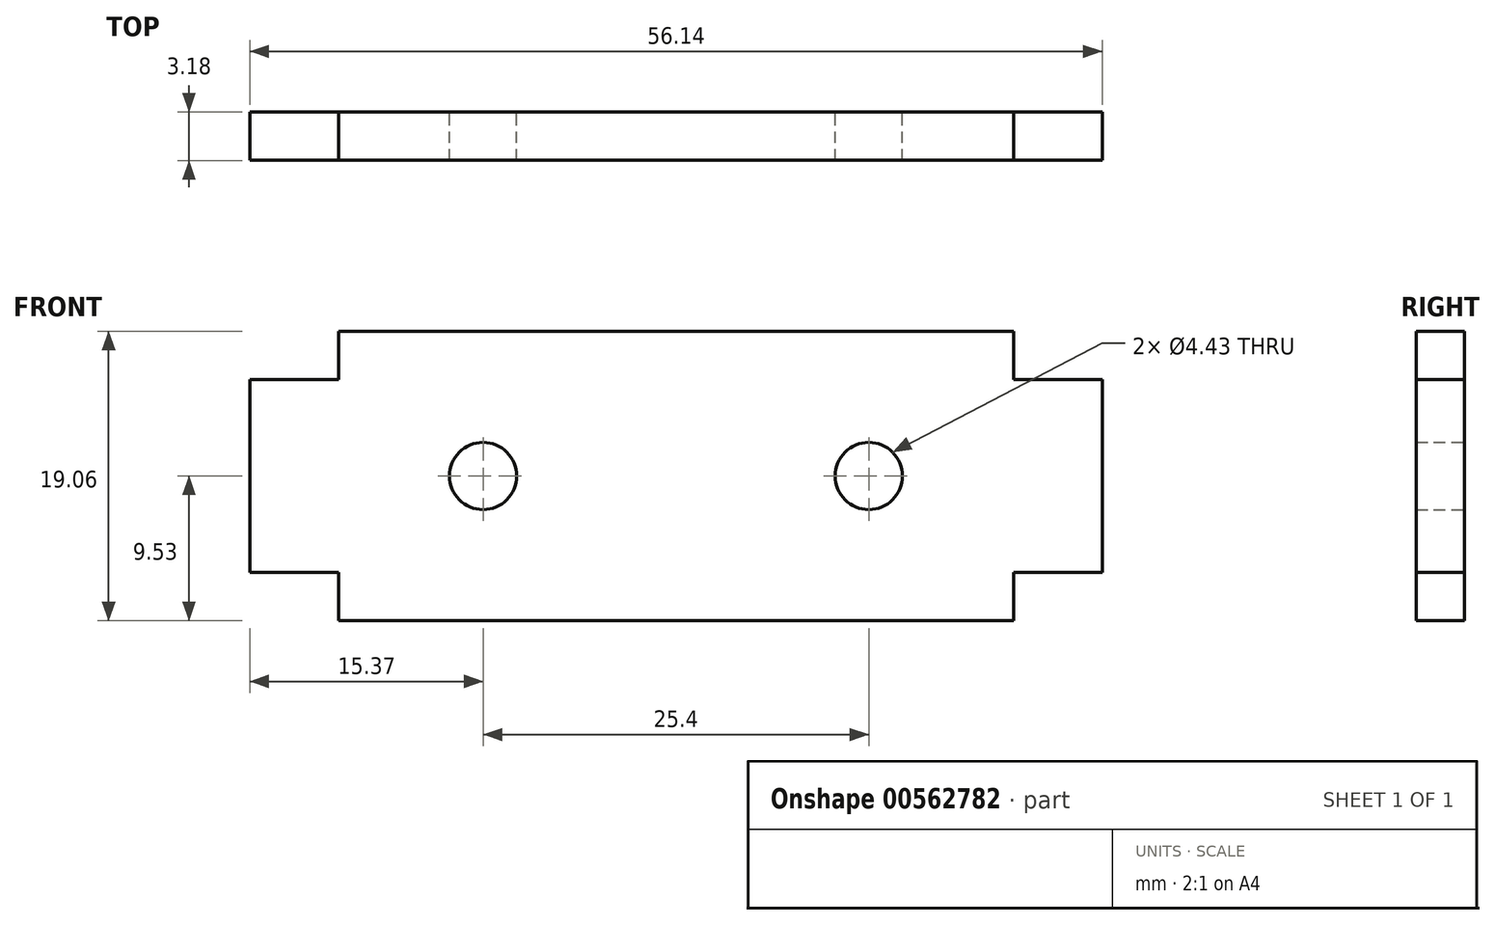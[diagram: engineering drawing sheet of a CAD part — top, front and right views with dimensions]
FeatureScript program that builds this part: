
annotation { "Feature Type Name" : "Feature", "Feature Type Description" : "" }
export const myFeature = defineFeature(function(context is Context, id is Id, definition is map)
    precondition{}
    {
        {
            var Q0;
            Q0=qCreatedBy(makeId("Front.planeOp"),FACE);
            var sketch = newSketch(context, id + "F0", { "sketchPlane" : qUnion([Q0])});
            skLineSegment(sketch, "E0.bottom", {"start": v(-22.23, 9.53) * mm, "end": v(22.23, 9.53) * mm});
            skLineSegment(sketch, "E0.top", {"start": v(-22.23, -9.52) * mm, "end": v(22.23, -9.52) * mm});
            skLineSegment(sketch, "E0.left", {"start": v(-22.23, 9.53) * mm, "end": v(-22.23, 6.35) * mm});
            skLineSegment(sketch, "E0.right", {"start": v(22.23, 9.53) * mm, "end": v(22.23, 6.35) * mm});
            skPoint(sketch, "E0.middle", {"position": v(0, 0) * mm});
            skCircle(sketch, "E1", {"center": v(-12.7, 0) * mm, "radius": 2.21 * mm});
            skCircle(sketch, "E2.MirrorC", {"center": v(12.7, 0) * mm, "radius": 2.21 * mm});
            skLineSegment(sketch, "E3.bottom", {"start": v(-22.23, 6.35) * mm, "end": v(-28.07, 6.35) * mm});
            skLineSegment(sketch, "E3.top", {"start": v(-22.23, -6.35) * mm, "end": v(-28.07, -6.35) * mm});
            skLineSegment(sketch, "E3.right", {"start": v(-28.07, 6.35) * mm, "end": v(-28.07, -6.35) * mm});
            skPoint(sketch, "E3.middle", {"position": v(-25.15, 0) * mm});
            skLineSegment(sketch, "E4.trimOffspring", {"start": v(-22.23, -6.35) * mm, "end": v(-22.23, -9.53) * mm});
            skLineSegment(sketch, "E5.MirrorCS", {"start": v(22.23, -6.35) * mm, "end": v(22.23, -9.53) * mm});
            skLineSegment(sketch, "E6.MirrorCS", {"start": v(28.07, 6.35) * mm, "end": v(28.07, -6.35) * mm});
            skLineSegment(sketch, "E7.MirrorCS", {"start": v(22.23, -6.35) * mm, "end": v(28.07, -6.35) * mm});
            skLineSegment(sketch, "E8.MirrorCS", {"start": v(22.23, 6.35) * mm, "end": v(28.07, 6.35) * mm});
            skPoint(sketch, "E9.MirrorP", {"position": v(25.15, 0) * mm});
            skSolve(sketch);
        }
        {
            var Q0;
            Q0 = qSketchRegion(id + "F0", true);
            extrude(context, id + "F1", {"entities" : qUnion([Q0]), "depth" : 3.17 * mm, "offsetDistance" : 25.4 * mm});
        }
    });
